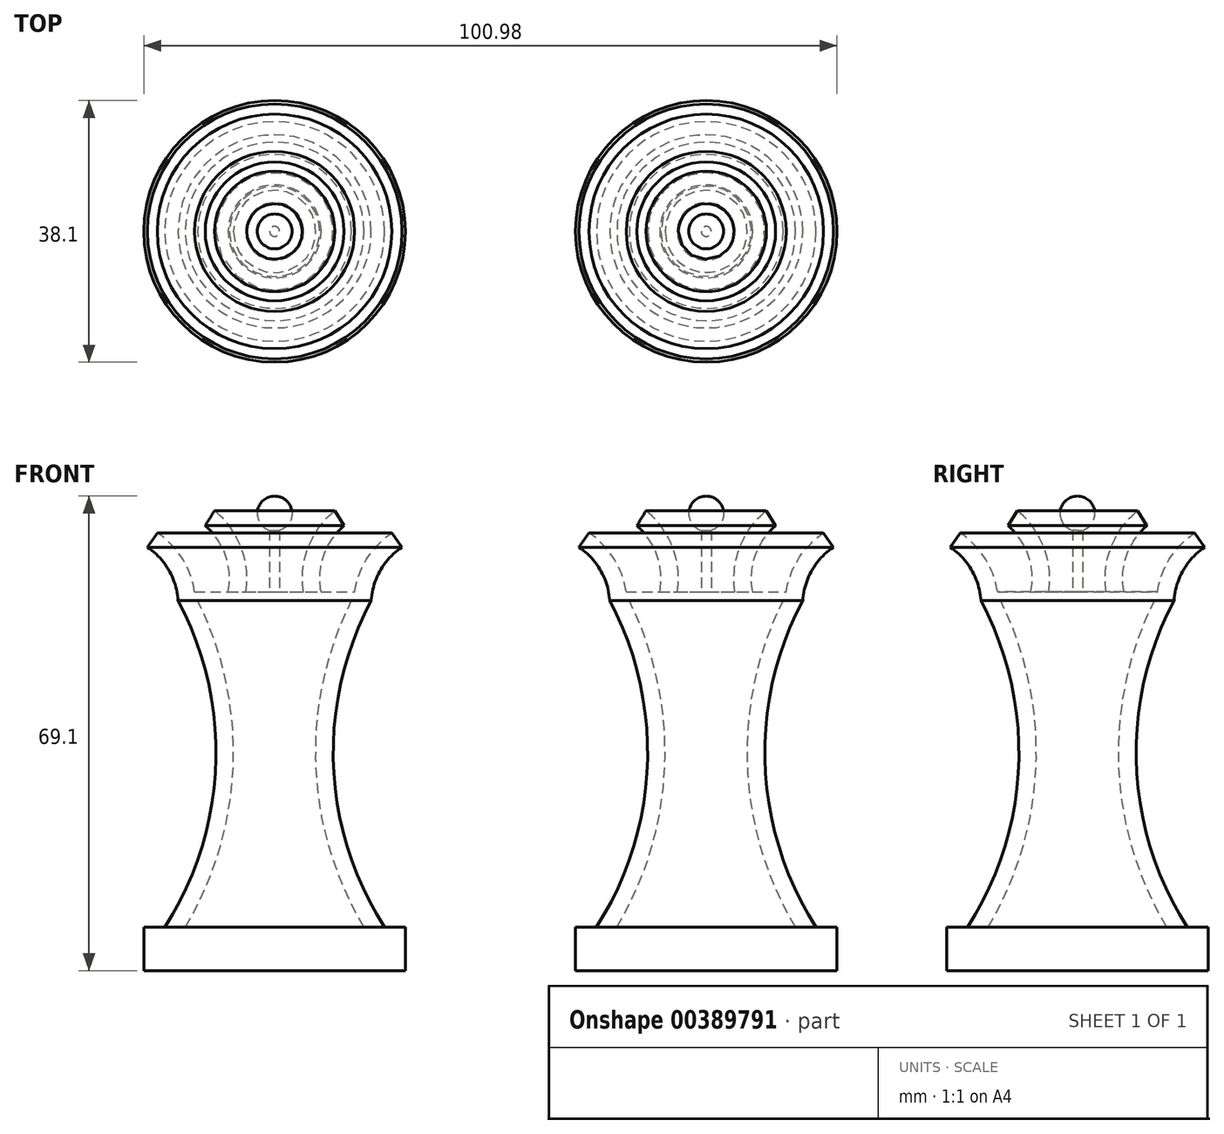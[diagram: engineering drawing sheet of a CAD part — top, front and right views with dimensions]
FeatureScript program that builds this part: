
annotation { "Feature Type Name" : "Feature", "Feature Type Description" : "" }
export const myFeature = defineFeature(function(context is Context, id is Id, definition is map)
    precondition{}
    {
        {
            var Q0;
            Q0=qCreatedBy(makeId("Front.planeOp"),FACE);
            var sketch = newSketch(context, id + "F0", { "sketchPlane" : qUnion([Q0])});
            skLineSegment(sketch, "E0.bottom", {"start": v(0, 0) * mm, "end": v(19.05, 0) * mm});
            skLineSegment(sketch, "E0.top", {"start": v(0, 6.35) * mm, "end": v(13, 6.35) * mm});
            skLineSegment(sketch, "E0.left", {"start": v(0, 0) * mm, "end": v(0, 6.35) * mm});
            skLineSegment(sketch, "E0.right", {"start": v(19.05, 0) * mm, "end": v(19.05, 6.35) * mm});
            skArc(sketch, "E1.0", {"start": v(14.06, 53.86) * mm, "mid": v(8.58, 29.84) * mm, "end": v(16, 6.35) * mm});
            skLineSegment(sketch, "E2", {"start": v(0, 53.86) * mm, "end": v(0, 66.56) * mm});
            skArc(sketch, "E3.0", {"start": v(11.2, 53.86) * mm, "mid": v(6.03, 29.87) * mm, "end": v(13, 6.35) * mm});
            skLineSegment(sketch, "E4", {"start": v(19.05, 6.35) * mm, "end": v(16, 6.35) * mm});
            skLineSegment(sketch, "E5", {"start": v(0, 53.86) * mm, "end": v(10.62, 53.86) * mm});
            skCircle(sketch, "E6", {"center": v(0, 66.56) * mm, "radius": 2.54 * mm});
            skLineSegment(sketch, "E7", {"start": v(0, 66.56) * mm, "end": v(0, 69.1) * mm});
            skLineSegment(sketch, "E8", {"start": v(0.73, 64.12) * mm, "end": v(0.73, 55.18) * mm});
            skArc(sketch, "E9", {"start": v(18.56, 61.66) * mm, "mid": v(15.4, 58.29) * mm, "end": v(14.06, 53.86) * mm});
            skArc(sketch, "E10.0", {"start": v(17.08, 63.73) * mm, "mid": v(13.48, 60.02) * mm, "end": v(11.66, 55.18) * mm});
            skArc(sketch, "E11", {"start": v(10.11, 64.79) * mm, "mid": v(7.15, 60.43) * mm, "end": v(6.77, 55.18) * mm});
            skArc(sketch, "E12.0", {"start": v(8.77, 66.97) * mm, "mid": v(4.9, 61.68) * mm, "end": v(4.2, 55.18) * mm});
            skLineSegment(sketch, "E13", {"start": v(18.56, 61.66) * mm, "end": v(17.08, 63.73) * mm});
            skLineSegment(sketch, "E14", {"start": v(10.11, 64.79) * mm, "end": v(8.77, 66.97) * mm});
            skLineSegment(sketch, "E15.bottom", {"start": v(0.73, 55.18) * mm, "end": v(4.2, 55.18) * mm});
            skLineSegment(sketch, "E15.top", {"start": v(0.73, 53.86) * mm, "end": v(11.2, 53.86) * mm});
            skLineSegment(sketch, "E16.trimOffspring", {"start": v(6.77, 55.18) * mm, "end": v(11.66, 55.18) * mm});
            skLineSegment(sketch, "E17.trimOffspring", {"start": v(11.2, 53.86) * mm, "end": v(10.62, 53.86) * mm});
            skLineSegment(sketch, "E18.bottom", {"start": v(62.88, 0) * mm, "end": v(81.93, 0) * mm});
            skLineSegment(sketch, "E18.top", {"start": v(62.88, 6.35) * mm, "end": v(75.9, 6.35) * mm});
            skLineSegment(sketch, "E18.left", {"start": v(62.88, 0) * mm, "end": v(62.88, 6.35) * mm});
            skLineSegment(sketch, "E18.right", {"start": v(81.93, 0) * mm, "end": v(81.93, 6.35) * mm});
            skArc(sketch, "E19.0", {"start": v(76.95, 53.86) * mm, "mid": v(71.46, 29.84) * mm, "end": v(78.88, 6.35) * mm});
            skLineSegment(sketch, "E20", {"start": v(62.88, 53.86) * mm, "end": v(62.88, 66.56) * mm});
            skArc(sketch, "E21.0", {"start": v(74.09, 53.86) * mm, "mid": v(68.92, 29.87) * mm, "end": v(75.9, 6.35) * mm});
            skLineSegment(sketch, "E22", {"start": v(81.93, 6.35) * mm, "end": v(78.88, 6.35) * mm});
            skLineSegment(sketch, "E23", {"start": v(62.88, 53.86) * mm, "end": v(73.5, 53.86) * mm});
            skCircle(sketch, "E24", {"center": v(62.88, 66.56) * mm, "radius": 2.54 * mm});
            skLineSegment(sketch, "E25", {"start": v(62.88, 66.56) * mm, "end": v(62.88, 69.1) * mm});
            skLineSegment(sketch, "E26", {"start": v(63.61, 64.12) * mm, "end": v(63.61, 55.18) * mm});
            skArc(sketch, "E27", {"start": v(81.44, 61.66) * mm, "mid": v(78.28, 58.29) * mm, "end": v(76.95, 53.86) * mm});
            skArc(sketch, "E28.0", {"start": v(79.96, 63.73) * mm, "mid": v(76.36, 60.02) * mm, "end": v(74.54, 55.18) * mm});
            skArc(sketch, "E29", {"start": v(73, 64.79) * mm, "mid": v(70.04, 60.43) * mm, "end": v(69.66, 55.18) * mm});
            skArc(sketch, "E30.0", {"start": v(71.65, 66.97) * mm, "mid": v(67.8, 61.68) * mm, "end": v(67.08, 55.18) * mm});
            skLineSegment(sketch, "E31", {"start": v(81.44, 61.66) * mm, "end": v(79.96, 63.73) * mm});
            skLineSegment(sketch, "E32", {"start": v(73, 64.79) * mm, "end": v(71.65, 66.97) * mm});
            skLineSegment(sketch, "E33.bottom", {"start": v(63.61, 55.18) * mm, "end": v(67.08, 55.18) * mm});
            skLineSegment(sketch, "E33.top", {"start": v(63.61, 53.86) * mm, "end": v(74.09, 53.86) * mm});
            skLineSegment(sketch, "E34.trimOffspring", {"start": v(69.66, 55.18) * mm, "end": v(74.54, 55.18) * mm});
            skLineSegment(sketch, "E35.trimOffspring", {"start": v(74.09, 53.86) * mm, "end": v(73.5, 53.86) * mm});
            skSolve(sketch);
        }
        {
            var Q0;
            Q0=makeQuery(id+"F0.imprint","IMPRINT",FACE,{"disambiguationData":[TD([[makeQuery(id+"F0.imprint","IMPRINT",EDGE,{"derivedFrom":sQuery(id+"F0.wireOp",EDGE,"E0.bottom")}),1.0]])]});
            var Q1;
            {var subQ0=sQuery(id+"F0.wireOp",EDGE,"E7");Q1=makeQuery(id+"F0.imprint","IMPRINT",FACE,{"disambiguationData":[TD([[makeQuery(id+"F0.imprint","IMPRINT",EDGE,{"derivedFrom":subQ0}),-1.0]])]});}
            var Q2;
            Q2=sQuery(id+"F0.wireOp",EDGE,"E0.left");
            revolve(context, id + "F1", {"entities" : qUnion([Q0, Q1]), "axis" : qUnion([Q2]), "revolveType" : RevolveType.FULL});
        }
        {
            var Q0;
            Q0=makeQuery(id+"F0.imprint","IMPRINT",FACE,{"disambiguationData":[TD([[makeQuery(id+"F0.imprint","IMPRINT",EDGE,{"derivedFrom":sQuery(id+"F0.wireOp",EDGE,"E18.bottom")}),1.0]])]});
            var Q1;
            {var subQ0=sQuery(id+"F0.wireOp",EDGE,"E25");Q1=makeQuery(id+"F0.imprint","IMPRINT",FACE,{"disambiguationData":[TD([[makeQuery(id+"F0.imprint","IMPRINT",EDGE,{"derivedFrom":subQ0}),-1.0]])]});}
            var Q2;
            Q2=sQuery(id+"F0.wireOp",EDGE,"E18.left");
            revolve(context, id + "F2", {"entities" : qUnion([Q0, Q1]), "axis" : qUnion([Q2]), "revolveType" : RevolveType.FULL});
        }
    });
